# Revit family: P190780JX-062c_JS42NXFXDE_Refrigeration_Built-in
name_source: partatom
category: Specialty Equipment
units: mm (PartAtom-declared; Revit-internal decimal feet)

## family parameters
Always vertical = Yes
Cut with Voids When Loaded = No
Enable Cutting in Views = No
Maintain Annotation Orientation = No
Part Type = Normal
Room Calculation Point = No
Round Connector Dimension = Use Diameter
Shared = No
Work Plane-Based = No

## types (1)
- JS42NXFXDE
    Accent Material = ARCAT - Metal - Steel - Black
    Amps = 0 A
    Body Material = ARCAT - Metal - Steel - Stainless
    Clearance Material = ARCAT - Clearance
    Connector Material = ARCAT - Metal - Cast Iron
    Default Elevation = 0"
    Depth = 27 3/8"
    Description = 42" Built-In Side-by-Side Refrigerator
Réfrigérateur côte à côte encastré Jenn-Air® de 42 pouces
    Dimension Guide = https://www.whirlpool.com
    Door Material = ARCAT - Thermal - Wood Fiber Cover Board
    Energy Guide = http://access.whirlpool.com
http://access.whirlpool.com Guide&sku=JS42NXFXDE&language=FR
    Family Name = 42" BIR side-by-side
    Feature 1 = Obsidian Interior
Intérieur noir obsidienne
    Feature 2 = Fully Flush, Fully Integrated Design
Conception entièrement intégrée, affleurante
    Feature 3 = Style with Custom Wood Panels or Suite-Coordinating Stainless Steel Panel Kits (not included)
Complétez le style à l'aide de panneaux personnalisés en bois ou de trousses de panneaux en acier inoxydable (non compris)
    Handle Material = ARCAT - Metal - Steel - Stainless
    Height = 83 1/8"
    Installation-Fabrication = http://access.whirlpool.com
http://access.whirlpool.com Instruction&sku=JS42NXFXDE&language=FR
    Leg Material = ARCAT - Plastic - Black
    Model = JS42NXFXDE
    Voltage = 0 V
    Width = 41 3/4"

## geometry (parser evidence)
native form markers: Sweep x3
no freeform markers — native parametric forms only
